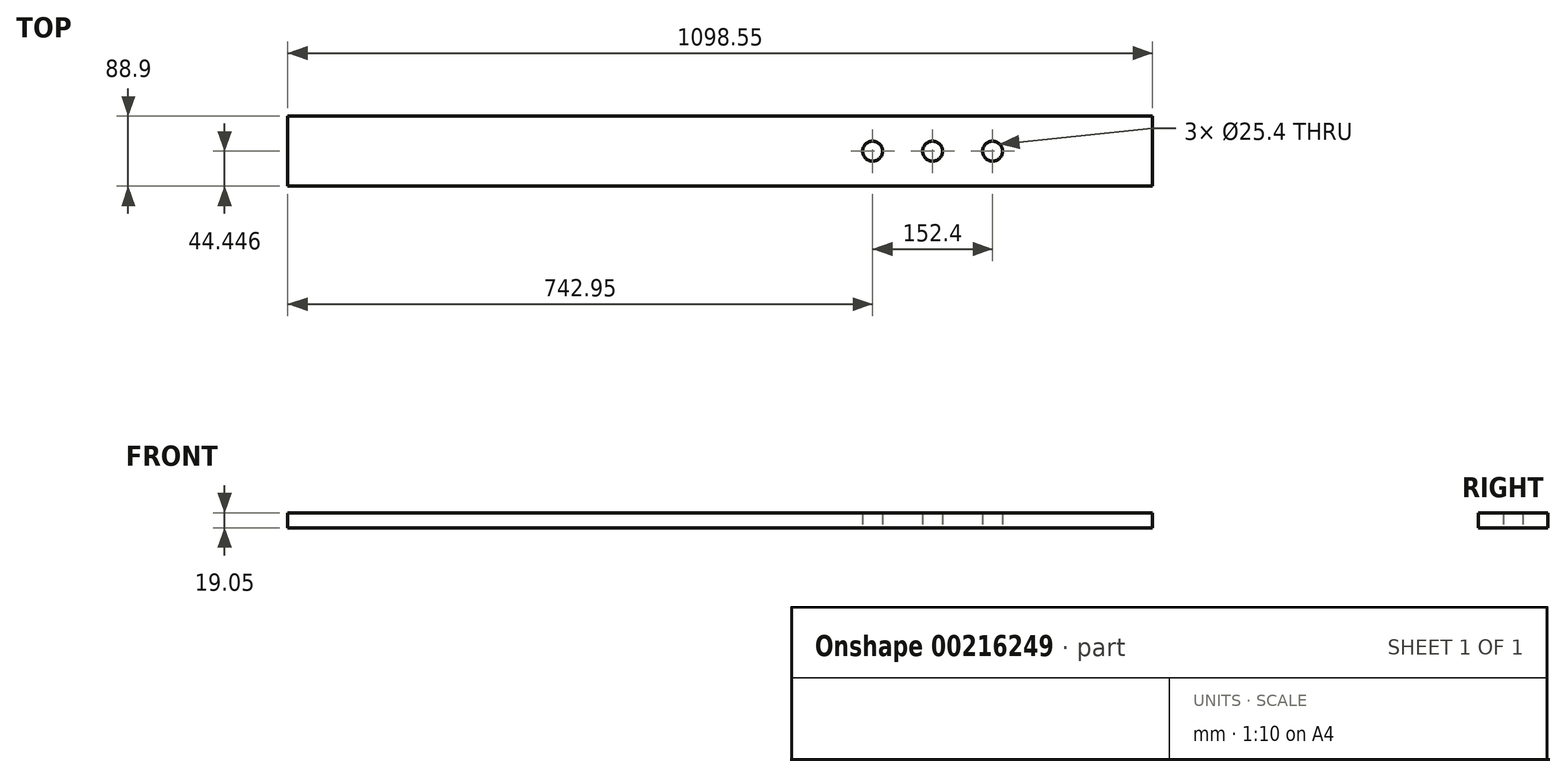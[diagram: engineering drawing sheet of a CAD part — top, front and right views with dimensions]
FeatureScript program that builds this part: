
annotation { "Feature Type Name" : "Feature", "Feature Type Description" : "" }
export const myFeature = defineFeature(function(context is Context, id is Id, definition is map)
    precondition{}
    {
        {
            var Q0;
            Q0=qCreatedBy(makeId("Top.planeOp"),FACE);
            var sketch = newSketch(context, id + "F0", { "sketchPlane" : qUnion([Q0])});
            skLineSegment(sketch, "E0", {"start": v(-3525.79, -68.02) * mm, "end": v(-2427.24, -68.02) * mm});
            skLineSegment(sketch, "E1", {"start": v(-2427.24, -68.02) * mm, "end": v(-2427.24, 20.88) * mm});
            skLineSegment(sketch, "E2", {"start": v(-2427.24, 20.88) * mm, "end": v(-3525.79, 20.88) * mm});
            skLineSegment(sketch, "E3", {"start": v(-3525.79, 20.88) * mm, "end": v(-3525.79, -68.02) * mm});
            skCircle(sketch, "E4", {"center": v(-2706.64, -23.57) * mm, "radius": 12.7 * mm});
            skCircle(sketch, "E5", {"center": v(-2630.44, -23.57) * mm, "radius": 12.7 * mm});
            skCircle(sketch, "E6", {"center": v(-2782.84, -23.57) * mm, "radius": 12.7 * mm});
            skSolve(sketch);
        }
        {
            var Q0;
            Q0=makeQuery(id+"F0.imprint","IMPRINT",FACE,{"disambiguationData":[TD([[makeQuery(id+"F0.imprint","IMPRINT",EDGE,{"derivedFrom":sQuery(id+"F0.wireOp",EDGE,"E0")}),1.0]])]});
            extrude(context, id + "F1", {"entities" : qUnion([Q0]), "depth" : 19.05 * mm});
        }
    });
